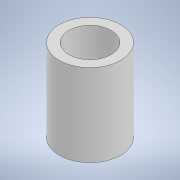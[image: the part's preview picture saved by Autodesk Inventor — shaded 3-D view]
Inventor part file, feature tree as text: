
AUTODESK INVENTOR PART (.ipt)
format: ipt  version: 2022 (Build 260153000, 153)  size: 117,760 bytes
history: native  units: in
note: dims shown in document units (in); Inventor stores cm internally (conversion verified against a paired STEP export)
features: extrude x3, sketch x3
ambient origin geometry x8: Origin, YZ Plane, XZ Plane, XY Plane, X Axis, Y Axis, Z Axis, Center Point
bodies: Solid1 (feature_tree)
feature tree (6):
  extrude  "Extrusion1"  Depth=0.2756in
  extrude  "Extrusion2"  Depth=0.1181in TaperAngle=0.0deg
  extrude  "Extrusion3"  Depth=0.22in
  sketch  "Sketch1"  dims[d0=0.1555in d1=0.2756in]
  sketch  "Sketch2"  dims[d2=0.0354in d3=0.1181in d4=0.0in]
  sketch  "Sketch3"  dims[d5=0.25in d6=0.0in d7=0.189in d8=0.22in d9=0.0in d10=0.18in d11=0.5in d12=0.0344in d13=0.5in d14=0.0344in]
